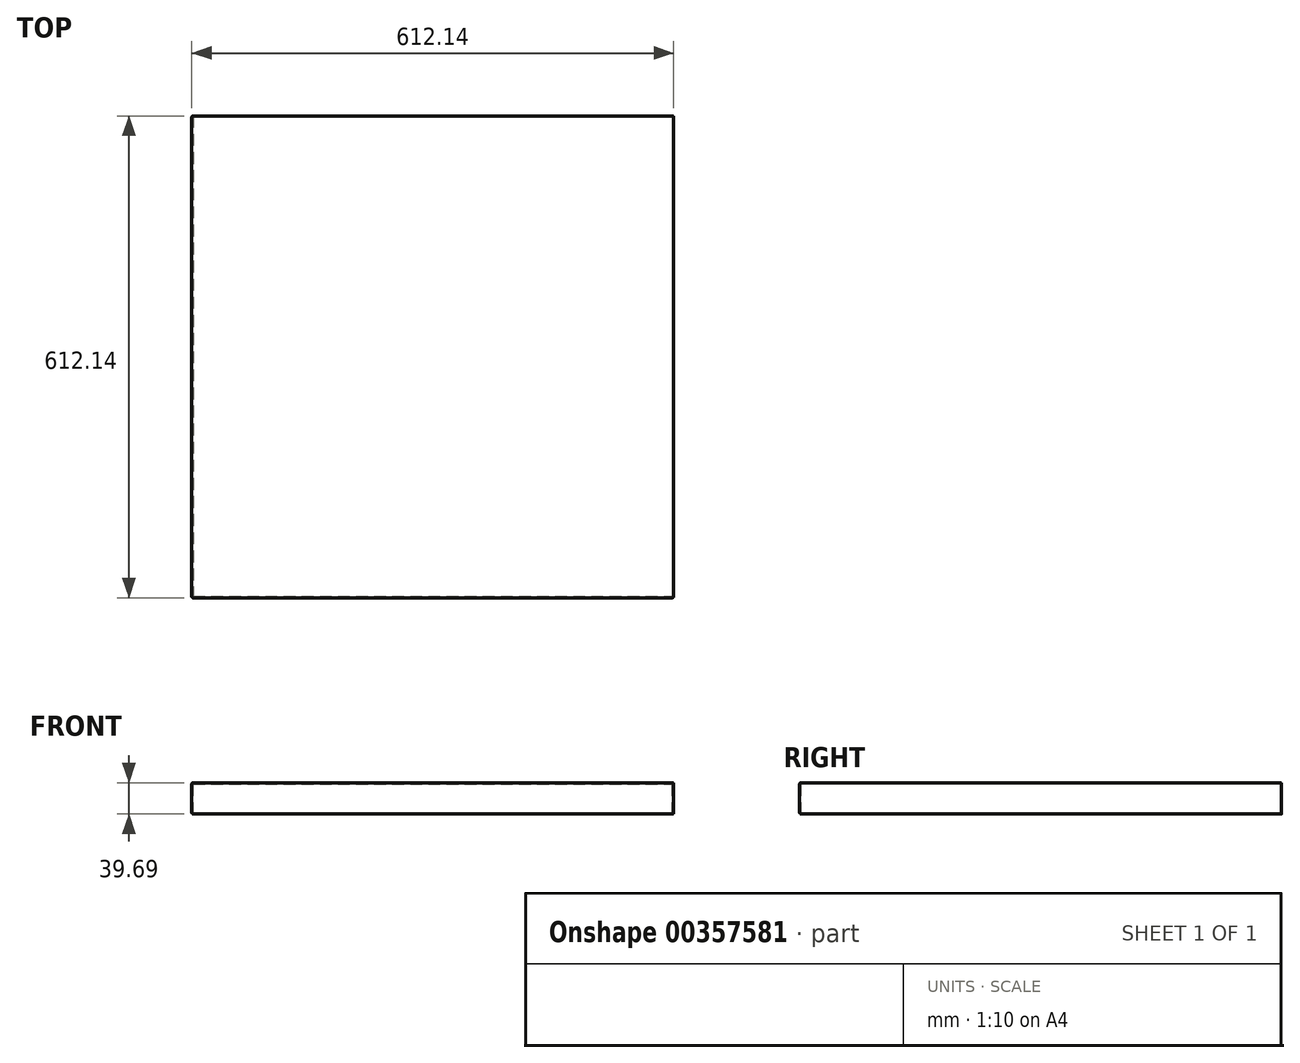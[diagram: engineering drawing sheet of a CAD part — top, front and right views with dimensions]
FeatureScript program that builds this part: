
annotation { "Feature Type Name" : "Feature", "Feature Type Description" : "" }
export const myFeature = defineFeature(function(context is Context, id is Id, definition is map)
    precondition{}
    {
        {
            var Q0;
            Q0=qCreatedBy(makeId("Top.planeOp"),FACE);
            var sketch = newSketch(context, id + "F0", { "sketchPlane" : qUnion([Q0])});
            skLineSegment(sketch, "E0.bottom", {"start": v(-306.07, 306.07) * mm, "end": v(306.07, 306.07) * mm});
            skLineSegment(sketch, "E0.top", {"start": v(-306.07, -306.07) * mm, "end": v(306.07, -306.07) * mm});
            skLineSegment(sketch, "E0.left", {"start": v(-306.07, 306.07) * mm, "end": v(-306.07, -306.07) * mm});
            skLineSegment(sketch, "E0.right", {"start": v(306.07, 306.07) * mm, "end": v(306.07, -306.07) * mm});
            skPoint(sketch, "E0.middle", {"position": v(0, 0) * mm});
            skSolve(sketch);
        }
        {
            var Q0;
            Q0=makeQuery(id+"F0.imprint","IMPRINT",FACE,{"disambiguationData":[TD([[makeQuery(id+"F0.imprint","IMPRINT",EDGE,{"derivedFrom":sQuery(id+"F0.wireOp",EDGE,"E0.bottom")}),-1.0]])]});
            extrude(context, id + "F1", {"entities" : qUnion([Q0]), "oppositeDirection" : true, "depth" : 1.59 * mm});
        }
        {
            var Q0;
            Q0=makeQuery(id+"F1.opExtrude","CAP_FACE",FACE,{"disambiguationData":[OSD([sQuery(id+"F0.wireOp",EDGE,"E0.bottom"),sQuery(id+"F0.wireOp",EDGE,"E0.top"),sQuery(id+"F0.wireOp",EDGE,"E0.left"),sQuery(id+"F0.wireOp",EDGE,"E0.right")])],"isStart":false});
            var sketch = newSketch(context, id + "F2", { "sketchPlane" : qUnion([Q0])});
            skLineSegment(sketch, "E1.0", {"start": v(304.48, -306.07) * mm, "end": v(306.07, -306.07) * mm});
            skLineSegment(sketch, "E2.0", {"start": v(306.07, -306.07) * mm, "end": v(306.07, 306.07) * mm});
            skLineSegment(sketch, "E3.0", {"start": v(-306.07, 306.07) * mm, "end": v(306.07, 306.07) * mm});
            skLineSegment(sketch, "E4.0", {"start": v(-306.07, -306.07) * mm, "end": v(-306.07, 306.07) * mm});
            skLineSegment(sketch, "E5.0", {"start": v(304.48, -306.07) * mm, "end": v(304.48, 304.48) * mm});
            skLineSegment(sketch, "E6.0", {"start": v(-304.48, -306.07) * mm, "end": v(-304.48, 304.48) * mm});
            skLineSegment(sketch, "E7.0", {"start": v(-304.48, 304.48) * mm, "end": v(304.48, 304.48) * mm});
            skLineSegment(sketch, "E8.0", {"start": v(-306.07, -306.07) * mm, "end": v(306.07, -306.07) * mm, "construction": true});
            skLineSegment(sketch, "E9", {"start": v(-304.48, -306.07) * mm, "end": v(-306.07, -306.07) * mm});
            skSolve(sketch);
        }
        {
            var Q0;
            Q0 = qSketchRegion(id + "F2", true);
            extrude(context, id + "F3", {"entities" : qUnion([Q0]), "operationType" : NewBodyOperationType.ADD, "depth" : 38.1 * mm});
        }
        {
            var Q0;
            Q0=makeQuery(id+"F1.opExtrude","CAP_EDGE",EDGE,{"disambiguationData":[OSD([sQuery(id+"F0.wireOp",EDGE,"E0.left")])],"isStart":true});
            fillet(context, id + "F4", {"entities" : qUnion([Q0]), "radius" : 1.6 * mm, "tangentPropagation" : true, "allowEdgeOverflow" : false});
        }
        {
            var Q0;
            Q0=makeQuery(id+"F1.opExtrude","CAP_EDGE",EDGE,{"disambiguationData":[OSD([sQuery(id+"F0.wireOp",EDGE,"E0.top")])],"isStart":true});
            fillet(context, id + "F5", {"entities" : qUnion([Q0]), "radius" : 1.6 * mm, "tangentPropagation" : true, "allowEdgeOverflow" : false});
        }
        {
            var Q0;
            Q0=makeQuery(id+"F3.boolean.opBoolean","MERGE",FACE,{"derivedFrom":[makeQuery(id+"F1.opExtrude","SWEPT_FACE",FACE,{"disambiguationData":[OSD([sQuery(id+"F0.wireOp",EDGE,"E0.left")])]}),makeQuery(id+"F3.opExtrude","SWEPT_FACE",FACE,{"disambiguationData":[OSD([sQuery(id+"F2.wireOp",EDGE,"E4.0")])]})]});
            fillet(context, id + "F6", {"entities" : qUnion([Q0]), "radius" : 1.59 * mm, "tangentPropagation" : true, "allowEdgeOverflow" : false});
        }
        {
            var Q0;
            Q0=makeQuery(id+"F3.boolean.opBoolean","MERGE",FACE,{"derivedFrom":[makeQuery(id+"F1.opExtrude","SWEPT_FACE",FACE,{"disambiguationData":[OSD([sQuery(id+"F0.wireOp",EDGE,"E0.right")])]}),makeQuery(id+"F3.opExtrude","SWEPT_FACE",FACE,{"disambiguationData":[OSD([sQuery(id+"F2.wireOp",EDGE,"E2.0")])]})]});
            fillet(context, id + "F7", {"entities" : qUnion([Q0]), "radius" : 1.59 * mm, "tangentPropagation" : true, "allowEdgeOverflow" : false});
        }
    });
